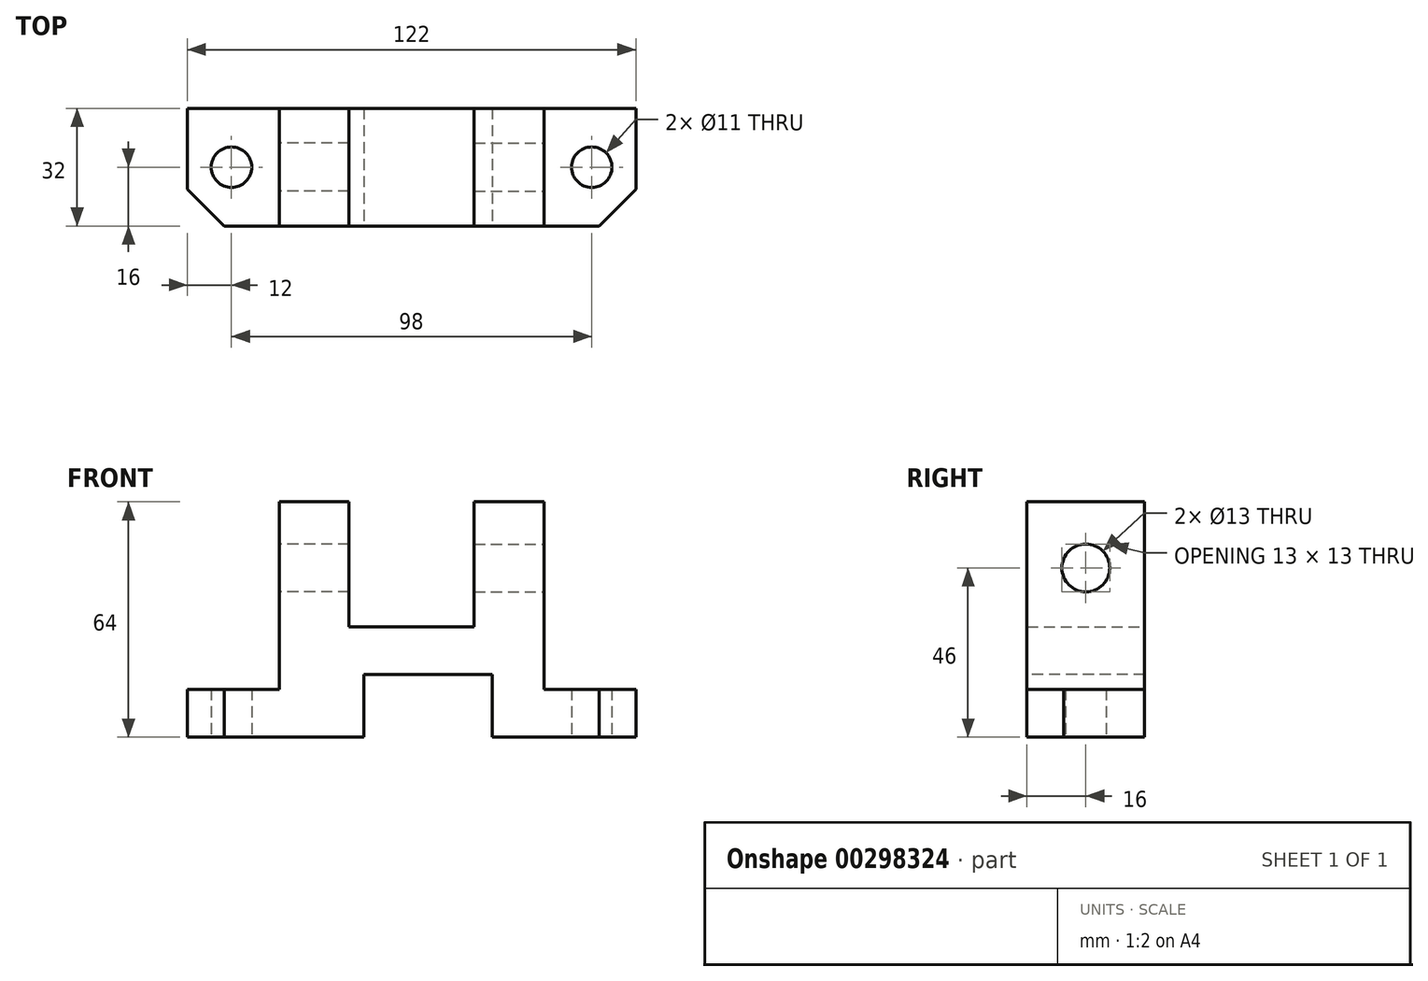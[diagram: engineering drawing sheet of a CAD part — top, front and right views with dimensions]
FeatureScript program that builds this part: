
annotation { "Feature Type Name" : "Feature", "Feature Type Description" : "" }
export const myFeature = defineFeature(function(context is Context, id is Id, definition is map)
    precondition{}
    {
        {
            var Q0;
            Q0=qCreatedBy(makeId("Top.planeOp"),FACE);
            var sketch = newSketch(context, id + "F0", { "sketchPlane" : qUnion([Q0])});
            skLineSegment(sketch, "E0.bottom", {"start": v(0, 0) * mm, "end": v(15, 0) * mm});
            skLineSegment(sketch, "E0.top", {"start": v(0, 32) * mm, "end": v(25, 32) * mm});
            skLineSegment(sketch, "E0.left", {"start": v(0, 0) * mm, "end": v(0, 32) * mm});
            skLineSegment(sketch, "E0.right", {"start": v(25, 10) * mm, "end": v(25, 32) * mm});
            skPoint(sketch, "E1", {"position": v(15, 0) * mm});
            skPoint(sketch, "E2", {"position": v(25, 10) * mm});
            skLineSegment(sketch, "E3", {"start": v(25, 10) * mm, "end": v(15, 0) * mm});
            skPoint(sketch, "E4", {"position": v(0, 16) * mm});
            skPoint(sketch, "E5", {"position": v(13, 16) * mm});
            skCircle(sketch, "E6", {"center": v(13, 16) * mm, "radius": 5.5 * mm});
            skSolve(sketch);
        }
        {
            var Q0;
            Q0 = qSketchRegion(id + "F0", true);
            extrude(context, id + "F1", {"entities" : qUnion([Q0]), "depth" : 13 * mm});
        }
        {
            var Q0;
            Q0=qCreatedBy(makeId("Top.planeOp"),FACE);
            var sketch = newSketch(context, id + "F2", { "sketchPlane" : qUnion([Q0])});
            skLineSegment(sketch, "E7.bottom", {"start": v(0, 0) * mm, "end": v(-19, 0) * mm});
            skLineSegment(sketch, "E7.top", {"start": v(0, 32) * mm, "end": v(-19, 32) * mm});
            skLineSegment(sketch, "E7.left", {"start": v(0, 0) * mm, "end": v(0, 32) * mm});
            skLineSegment(sketch, "E7.right", {"start": v(-19, 0) * mm, "end": v(-19, 32) * mm});
            skSolve(sketch);
        }
        {
            var Q0;
            Q0 = qSketchRegion(id + "F2", true);
            extrude(context, id + "F3", {"entities" : qUnion([Q0]), "operationType" : NewBodyOperationType.ADD, "depth" : 64 * mm});
        }
        {
            var Q0;
            Q0=makeQuery(id+"F3.opExtrude","SWEPT_FACE",FACE,{"disambiguationData":[OSD([sQuery(id+"F2.wireOp",EDGE,"E7.left")])]});
            var sketch = newSketch(context, id + "F4", { "sketchPlane" : qUnion([Q0])});
            skPoint(sketch, "E8", {"position": v(16, 46) * mm});
            skCircle(sketch, "E9", {"center": v(16, 46) * mm, "radius": 6.5 * mm});
            skSolve(sketch);
        }
        {
            var Q0;
            Q0 = qSketchRegion(id + "F4", true);
            extrude(context, id + "F5", {"entities" : qUnion([Q0]), "operationType" : NewBodyOperationType.REMOVE, "endBound" : BoundingType.UP_TO_NEXT, "oppositeDirection" : true, "depth" : 25 * mm});
        }
        {
            var Q0;
            Q0=qCreatedBy(makeId("Top.planeOp"),FACE);
            var sketch = newSketch(context, id + "F6", { "sketchPlane" : qUnion([Q0])});
            skLineSegment(sketch, "E10.bottom", {"start": v(-19, 0) * mm, "end": v(-36, 0) * mm});
            skLineSegment(sketch, "E10.top", {"start": v(-19, 32) * mm, "end": v(-36, 32) * mm});
            skLineSegment(sketch, "E10.left", {"start": v(-19, 0) * mm, "end": v(-19, 32) * mm});
            skLineSegment(sketch, "E10.right", {"start": v(-36, 0) * mm, "end": v(-36, 32) * mm});
            skSolve(sketch);
        }
        {
            var Q0;
            Q0 = qSketchRegion(id + "F6", true);
            extrude(context, id + "F7", {"entities" : qUnion([Q0]), "operationType" : NewBodyOperationType.ADD, "depth" : 30 * mm});
        }
        {
            var Q0;
            Q0=makeQuery(id+"F7.opExtrude","SWEPT_FACE",FACE,{"disambiguationData":[OSD([sQuery(id+"F6.wireOp",EDGE,"E10.right")])]});
            cPlane(context, id + "F8", {"entities" : qUnion([Q0]), "cplaneType" : CPlaneType.OFFSET, "offset" : 0 * mm, "width" : 150 * mm, "height" : 150 * mm});
        }
        {
            var Q0;
            Q0=makeQuery(id+"F1.opExtrude","SWEPT_BODY",BODY,{"disambiguationData":[OSD([sQuery(id+"F0.wireOp",EDGE,"E0.bottom"),sQuery(id+"F0.wireOp",EDGE,"E0.top"),sQuery(id+"F0.wireOp",EDGE,"E0.left"),sQuery(id+"F0.wireOp",EDGE,"E0.right"),sQuery(id+"F0.wireOp",EDGE,"E3"),sQuery(id+"F0.wireOp",EDGE,"E6")])]});
            var Q1;
            Q1=qCreatedBy(id+"F8.planeOp",FACE);
            mirror(context, id + "F9", {"operationType" : NewBodyOperationType.ADD, "entities" : qUnion([Q0]), "mirrorPlane" : qUnion([Q1])});
        }
        {
            var Q0;
            {var subQ0=makeQuery(id+"F7.boolean.opBoolean","MERGE",FACE,{"derivedFrom":[makeQuery(id+"F3.boolean.opBoolean","MERGE",FACE,{"derivedFrom":[makeQuery(id+"F1.opExtrude","SWEPT_FACE",FACE,{"disambiguationData":[OSD([sQuery(id+"F0.wireOp",EDGE,"E0.bottom")])]}),makeQuery(id+"F3.opExtrude","SWEPT_FACE",FACE,{"disambiguationData":[OSD([sQuery(id+"F2.wireOp",EDGE,"E7.bottom")])]})]}),makeQuery(id+"F7.opExtrude","SWEPT_FACE",FACE,{"disambiguationData":[OSD([sQuery(id+"F6.wireOp",EDGE,"E10.bottom")])]})]});Q0=makeQuery(id+"F9.boolean.opBoolean","MERGE",FACE,{"derivedFrom":[subQ0,makeQuery(id+"F9.opPattern","COPY",FACE,{"derivedFrom":subQ0,"instanceName":"1"})]});}
            var sketch = newSketch(context, id + "F10", { "sketchPlane" : qUnion([Q0])});
            skPoint(sketch, "E11", {"position": v(-14, 0) * mm});
            skLineSegment(sketch, "E12.bottom", {"start": v(-14, 0) * mm, "end": v(-49, 0) * mm});
            skLineSegment(sketch, "E12.top", {"start": v(-14, 17) * mm, "end": v(-49, 17) * mm});
            skLineSegment(sketch, "E12.left", {"start": v(-14, 0) * mm, "end": v(-14, 17) * mm});
            skLineSegment(sketch, "E12.right", {"start": v(-49, 0) * mm, "end": v(-49, 17) * mm});
            skSolve(sketch);
        }
        {
            var Q0;
            Q0=makeQuery(id+"F10.imprint","IMPRINT",FACE,{"disambiguationData":[TD([[makeQuery(id+"F10.imprint","IMPRINT",EDGE,{"derivedFrom":sQuery(id+"F10.wireOp",EDGE,"E12.bottom")}),1.0]])]});
            extrude(context, id + "F11", {"entities" : qUnion([Q0]), "operationType" : NewBodyOperationType.REMOVE, "endBound" : BoundingType.UP_TO_NEXT, "oppositeDirection" : true, "depth" : 25 * mm});
        }
    });
